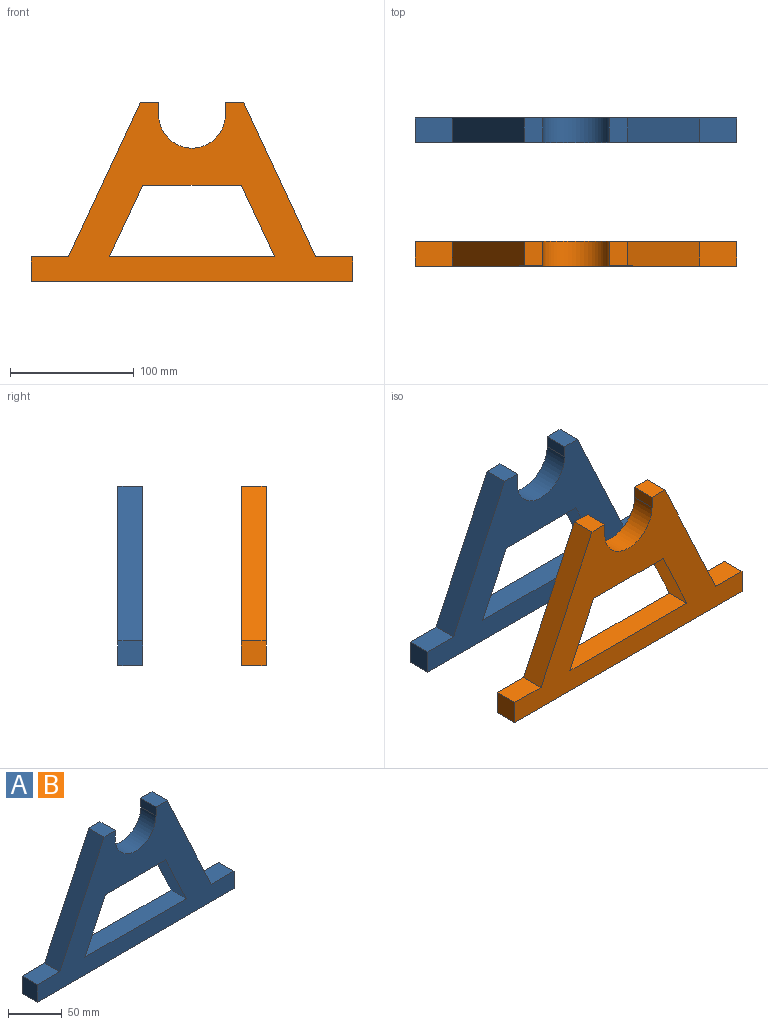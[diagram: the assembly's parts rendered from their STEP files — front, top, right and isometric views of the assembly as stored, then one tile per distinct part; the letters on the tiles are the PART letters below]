
ASSEMBLY  parts=2 mates=2
PART A: 18 faces, bbox 260x20x145 mm
  f0: plane 20x14.71mm, normal (0,0,1), area 294.2mm2, adj f1,f15,f16,f17
  f1: plane 125x58.29mm, normal (-0.91,0,0.42), area 2758.4mm2, adj f0,f2,f16,f17
  f2: plane 30x20mm, normal (0,0,1), area 600mm2, adj f1,f3,f16,f17
  f3: plane 20x20mm, normal (-1,0,0), area 400mm2, adj f2,f4,f16,f17
  f4: plane 260x20mm, normal (0,0,-1), area 5200mm2, adj f3,f5,f16,f17
  f5: plane 20x20mm, normal (1,0,0), area 400mm2, adj f4,f6,f16,f17
  f6: plane 30x20mm, normal (0,0,1), area 600mm2, adj f5,f7,f16,f17
  f7: plane 125x58.29mm, normal (0.91,0,0.42), area 2758.4mm2, adj f6,f8,f16,f17
  f8: plane 20x14.71mm, normal (0,0,1), area 294.2mm2, adj f7,f9,f16,f17
  f9: plane 20x10mm, normal (-1,0,0), area 200mm2, adj f8,f10,f16,f17
  f10: cylinder r=27mm len=54mm, axis (0,1,0), area 1696.5mm2, adj f9,f15,f16,f17
  f11: plane 133.8x20mm, normal (0,0,1), area 2675.9mm2, adj f12,f14,f16,f17
  f12: plane 58x27.05mm, normal (0.91,0,-0.42), area 1279.9mm2, adj f11,f13,f16,f17
  f13: plane 79.71x20mm, normal (0,0,-1), area 1594.1mm2, adj f12,f14,f16,f17
  f14: plane 58x27.05mm, normal (-0.91,0,-0.42), area 1279.9mm2, adj f11,f13,f16,f17
  f15: plane 20x10mm, normal (1,0,0), area 200mm2, adj f0,f10,f16,f17
  f16: plane 260x145mm, normal (0,-1,0), area 15037.2mm2, adj f0,f1,f2,f3,f4,f5,f6,f7
  f17: plane 260x145mm, normal (0,1,0), area 15037.2mm2, adj f0,f1,f2,f3,f4,f5,f6,f7
PART B: same geometry as A
PLACE A t=(-79.14,226.45,-52.79)mm
PLACE B t=(-79.14,126.45,-52.79)mm
MATE planar A.f4 <-> B.f4  axis (0,0,-1) through (-79.14,216.45,-52.79)mm
MATE cylindrical B.f10 <-> A.f10  axis (0,1,0) through (-79.14,106.45,82.21)mm
